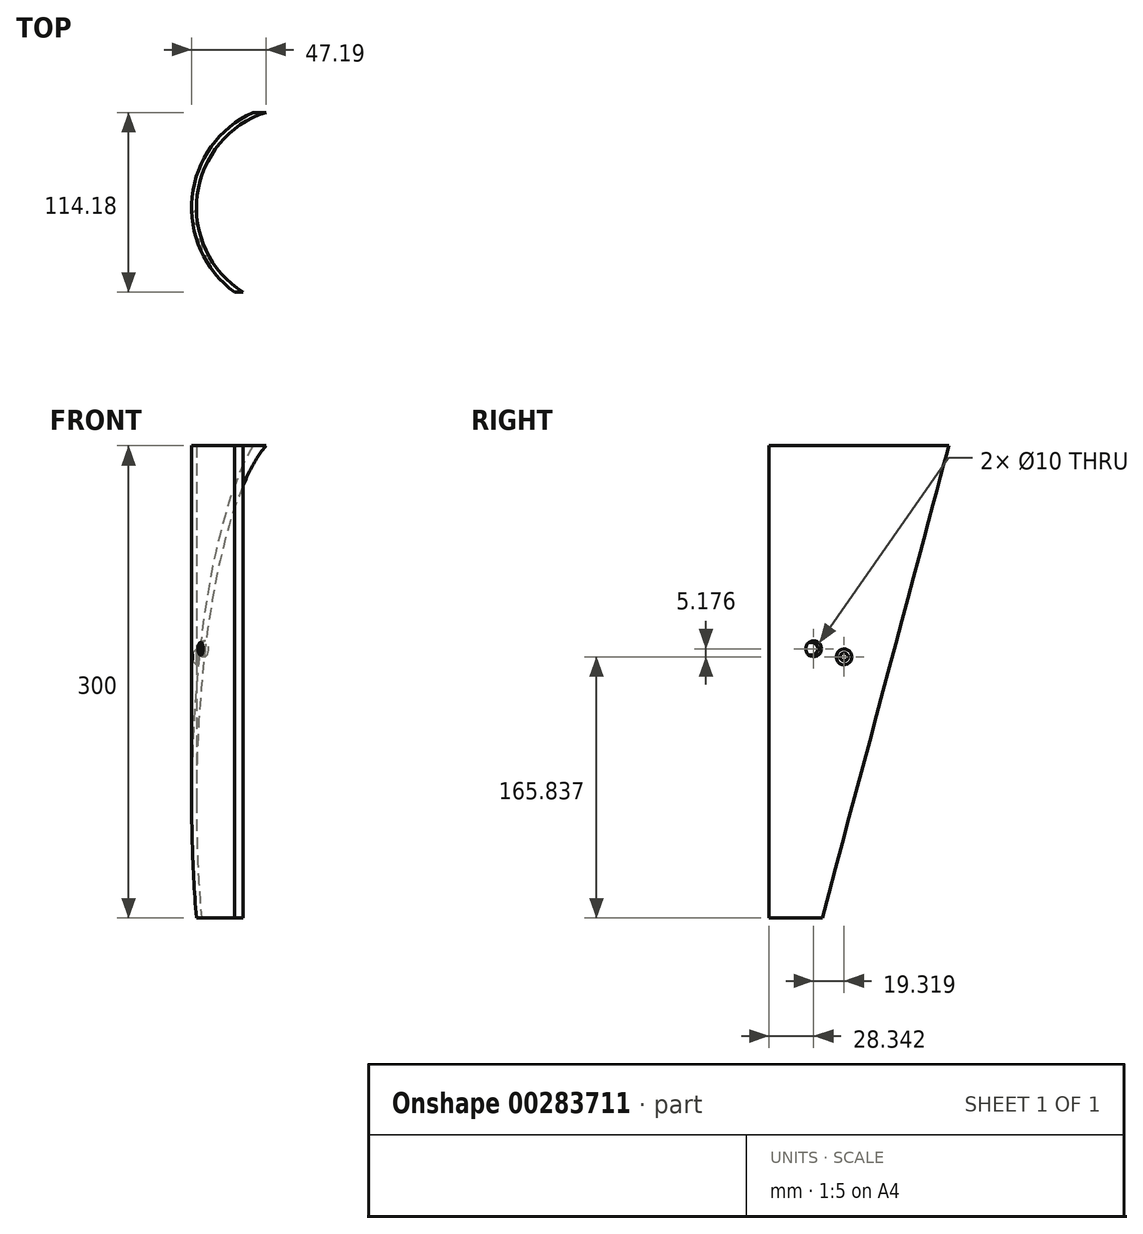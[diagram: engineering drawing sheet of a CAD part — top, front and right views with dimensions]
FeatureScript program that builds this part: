
annotation { "Feature Type Name" : "Feature", "Feature Type Description" : "" }
export const myFeature = defineFeature(function(context is Context, id is Id, definition is map)
    precondition{}
    {
        {
            var Q0;
            Q0=qCreatedBy(makeId("Top.planeOp"),FACE);
            var sketch = newSketch(context, id + "F0", { "sketchPlane" : qUnion([Q0])});
            skCircle(sketch, "E0", {"center": v(0, 0) * mm, "radius": 63.5 * mm});
            skCircle(sketch, "E1.0", {"center": v(0, 0) * mm, "radius": 66.5 * mm});
            skSolve(sketch);
        }
        {
            var Q0;
            Q0=makeQuery(id+"F0.imprint","IMPRINT",FACE,{"disambiguationData":[TD([[makeQuery(id+"F0.imprint","IMPRINT",EDGE,{"derivedFrom":sQuery(id+"F0.wireOp",EDGE,"E0")}),-1.0]])]});
            extrude(context, id + "F1", {"entities" : qUnion([Q0]), "depth" : 300 * mm});
        }
        {
            var Q0;
            Q0=qCreatedBy(makeId("Right.planeOp"),FACE);
            cPlane(context, id + "F2", {"entities" : qUnion([Q0]), "cplaneType" : CPlaneType.OFFSET, "offset" : 126 * mm, "width" : 150 * mm, "height" : 150 * mm});
        }
        {
            var Q0;
            Q0=qCreatedBy(id+"F2.planeOp",FACE);
            var sketch = newSketch(context, id + "F3", { "sketchPlane" : qUnion([Q0])});
            skLineSegment(sketch, "E2", {"start": v(-53.69, 300) * mm, "end": v(60.5, 300) * mm});
            skLineSegment(sketch, "E3", {"start": v(60.5, 300) * mm, "end": v(-19.9, 0) * mm});
            skLineSegment(sketch, "E4", {"start": v(-19.9, 0) * mm, "end": v(-53.69, 0) * mm});
            skLineSegment(sketch, "E5", {"start": v(-53.69, 0) * mm, "end": v(-53.69, 300) * mm});
            skSolve(sketch);
        }
        {
            var Q0;
            Q0=makeQuery(id+"F3.imprint","IMPRINT",FACE,{"disambiguationData":[TD([[makeQuery(id+"F3.imprint","IMPRINT",EDGE,{"derivedFrom":sQuery(id+"F3.wireOp",EDGE,"E2")}),-1.0]])]});
            extrude(context, id + "F4", {"entities" : qUnion([Q0]), "operationType" : NewBodyOperationType.INTERSECT, "endBound" : BoundingType.THROUGH_ALL, "oppositeDirection" : true, "depth" : 25 * mm});
        }
        {
            var Q0;
            Q0=makeQuery(id+"F4.boolean.opBoolean","SPLIT",BODY,{"disambiguationData":[OD(0.0)],"derivedFrom":makeQuery(id+"F1.opExtrude","SWEPT_BODY",BODY,{"disambiguationData":[OSD([sQuery(id+"F0.wireOp",EDGE,"E0"),sQuery(id+"F0.wireOp",EDGE,"E1.0")])]})});
            deleteBodies(context, id + "F5", {"entities" : qUnion([Q0])});
        }
        {
            var Q0;
            Q0=qCreatedBy(id+"F2.planeOp",FACE);
            var sketch = newSketch(context, id + "F6", { "sketchPlane" : qUnion([Q0])});
            skPoint(sketch, "E6", {"position": v(-6.03, 165.84) * mm});
            skPoint(sketch, "E7", {"position": v(-25.35, 171.01) * mm});
            skLineSegment(sketch, "E8", {"start": v(-6.03, 165.84) * mm, "end": v(-25.35, 165.84) * mm, "construction": true});
            skLineSegment(sketch, "E9", {"start": v(-25.35, 165.84) * mm, "end": v(-25.35, 171.01) * mm, "construction": true});
            skLineSegment(sketch, "E10", {"start": v(-25.35, 171.01) * mm, "end": v(-6.03, 165.84) * mm, "construction": true});
            skLineSegment(sketch, "E11.bottom", {"start": v(4.93, 175.84) * mm, "end": v(-94.21, 202.4) * mm});
            skLineSegment(sketch, "E11.top", {"start": v(-1.54, 151.7) * mm, "end": v(-100.68, 178.26) * mm});
            skLineSegment(sketch, "E11.left", {"start": v(4.93, 175.84) * mm, "end": v(-1.54, 151.7) * mm});
            skLineSegment(sketch, "E11.right", {"start": v(-94.21, 202.4) * mm, "end": v(-100.68, 178.26) * mm});
            skSolve(sketch);
        }
        {
            var Q0;
            Q0 = qSketchRegion(id + "F6", true);
            extrude(context, id + "F7", {"entities" : qUnion([Q0]), "operationType" : NewBodyOperationType.REMOVE, "oppositeDirection" : true, "depth" : 61.1 * mm});
        }
        {
            var Q0;
            Q0=sQuery(id+"F6.wireOp",VERTEX,"E7");
            var Q1;
            Q1=sQuery(id+"F6.wireOp",VERTEX,"E6");
            var Q2;
            Q2=makeQuery(id+"F4.boolean.opBoolean","SPLIT",BODY,{"disambiguationData":[OD(1.0)],"derivedFrom":makeQuery(id+"F1.opExtrude","SWEPT_BODY",BODY,{"disambiguationData":[OSD([sQuery(id+"F0.wireOp",EDGE,"E0"),sQuery(id+"F0.wireOp",EDGE,"E1.0")])]})});
            hole(context, id + "F8", {"style" : HoleStyle.C_SINK, "endStyle" : HoleEndStyle.THROUGH, "holeDiameter" : 5 * mm, "cSinkDiameter" : 10 * mm, "cSinkAngle" : 90 * degree, "tappedDepth" : 12 * mm, "tapClearance" : 3, "locations" : qUnion([Q0, Q1]), "scope" : qUnion([Q2])});
        }
    });
